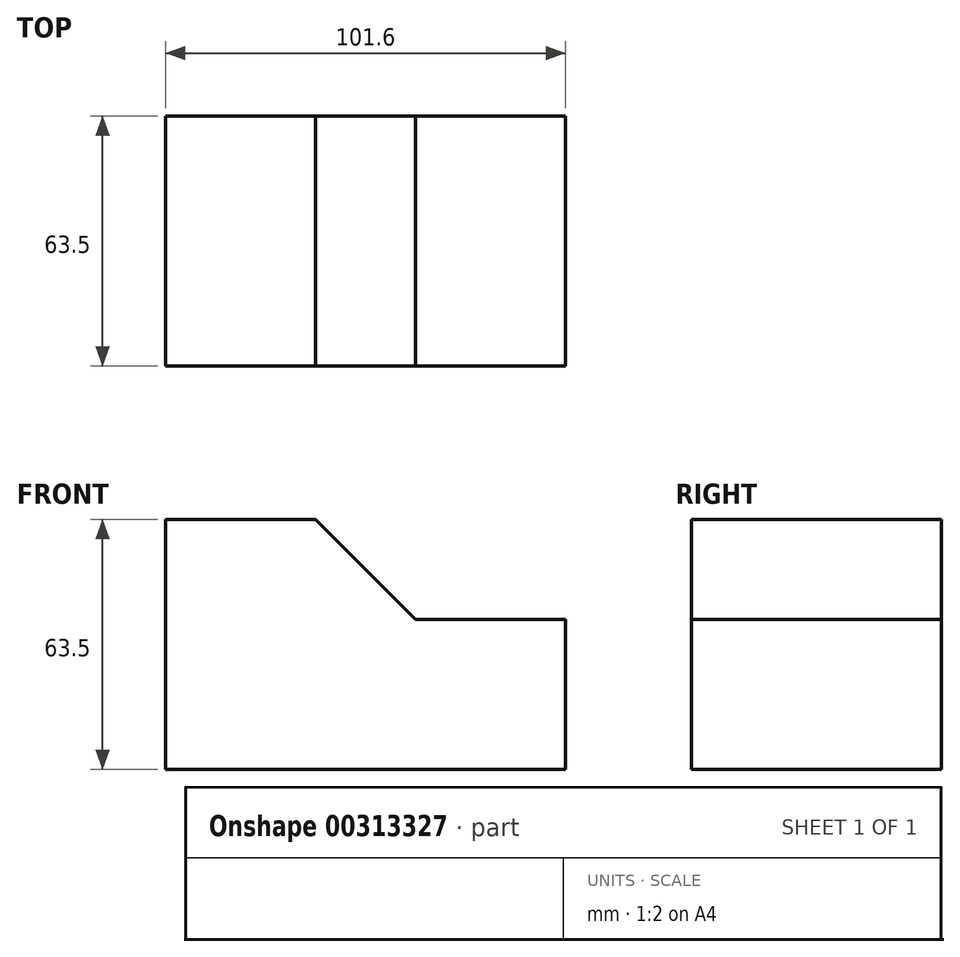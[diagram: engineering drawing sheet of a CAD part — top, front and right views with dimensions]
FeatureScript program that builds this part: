
annotation { "Feature Type Name" : "Feature", "Feature Type Description" : "" }
export const myFeature = defineFeature(function(context is Context, id is Id, definition is map)
    precondition{}
    {
        {
            var Q0;
            Q0=qCreatedBy(makeId("Front.planeOp"),FACE);
            var sketch = newSketch(context, id + "F0", { "sketchPlane" : qUnion([Q0])});
            skLineSegment(sketch, "E0", {"start": v(-43.72, 44.16) * mm, "end": v(-43.72, -19.34) * mm});
            skLineSegment(sketch, "E1", {"start": v(-43.72, 44.16) * mm, "end": v(-5.62, 44.16) * mm});
            skLineSegment(sketch, "E2", {"start": v(-43.72, -19.34) * mm, "end": v(57.88, -19.34) * mm});
            skLineSegment(sketch, "E3", {"start": v(-5.62, 44.16) * mm, "end": v(57.88, -19.34) * mm});
            skLineSegment(sketch, "E4", {"start": v(57.88, -19.34) * mm, "end": v(57.88, 18.76) * mm});
            skLineSegment(sketch, "E5", {"start": v(57.88, 18.76) * mm, "end": v(19.78, 18.76) * mm});
            skSolve(sketch);
        }
        {
            var Q0;
            Q0=makeQuery(id+"F0.imprint","IMPRINT",FACE,{"disambiguationData":[TD([[makeQuery(id+"F0.imprint","IMPRINT",EDGE,{"derivedFrom":sQuery(id+"F0.wireOp",EDGE,"E0")}),1.0]])]});
            var Q1;
            {var subQ0=sQuery(id+"F0.wireOp",EDGE,"E4");Q1=makeQuery(id+"F0.imprint","IMPRINT",FACE,{"disambiguationData":[TD([[makeQuery(id+"F0.imprint","IMPRINT",EDGE,{"derivedFrom":subQ0}),1.0]])]});}
            extrude(context, id + "F1", {"entities" : qUnion([Q0, Q1]), "depth" : 63.5 * mm});
        }
    });
